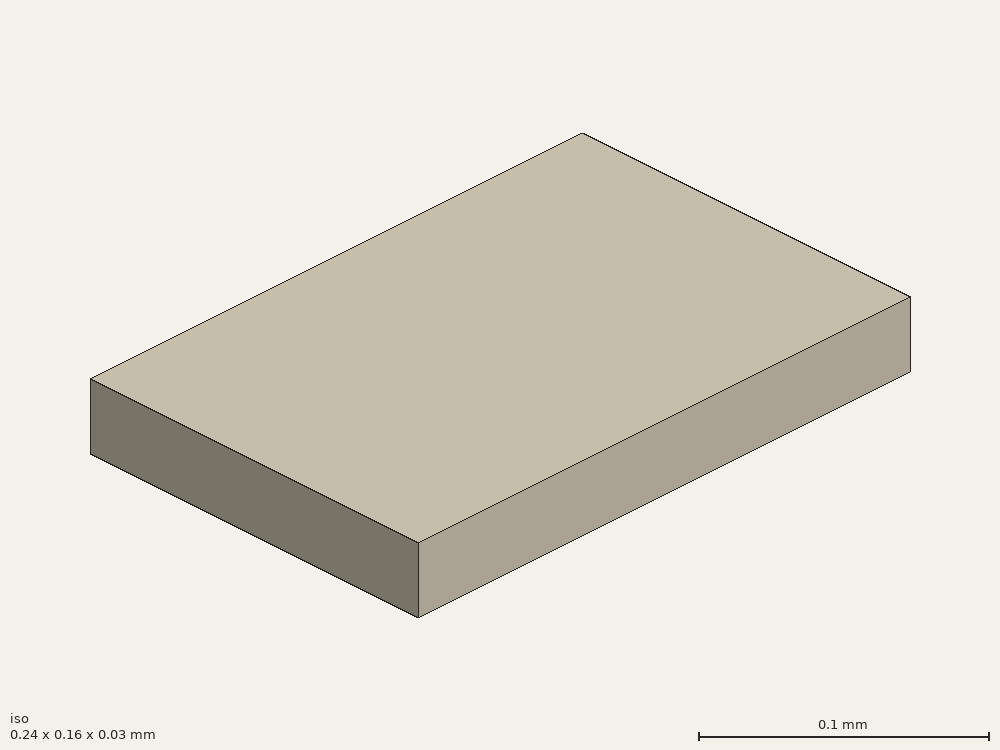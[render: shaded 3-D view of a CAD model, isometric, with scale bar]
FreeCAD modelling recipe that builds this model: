
FCSTD DOCUMENT  (FreeCAD 0.15R4671 (Git))
Label: quadrangle3
License: All rights reserved
LicenseURL: http://en.wikipedia.org/wiki/All_rights_reserved
objects: Sketcher::SketchObject×1, PartDesign::Pad×1
note: 3 computed .brp shape members not serialized (recipe doc carries the construction recipe); baked Part::Feature solids carry a one-line shape summary decoded from their .brp

FEATURE [Sketcher::SketchObject] Sketch
  sketch-geometry (4):
    g0: LineSegment StartX=0.12 StartY=0.08 StartZ=0 EndX=-0.12 EndY=0.08 EndZ=0
    g1: LineSegment StartX=-0.12 StartY=0.08 StartZ=0 EndX=-0.12 EndY=-0.08 EndZ=0
    g2: LineSegment StartX=-0.12 StartY=-0.08 StartZ=0 EndX=0.12 EndY=-0.08 EndZ=0
    g3: LineSegment StartX=0.12 StartY=-0.08 StartZ=0 EndX=0.12 EndY=0.08 EndZ=0
  constraints (13):
    c: Coincident(g0,g1)
    c: Coincident(g1,g2)
    c: Coincident(g2,g3)
    c: Coincident(g3,g0)
    c: Horizontal(g0)
    c: Horizontal(g2)
    c: Vertical(g1)
    c: Vertical(g3)
    c: Symmetric(g0,g2,g-1)
    c: Equal(g0,g2)
    c: Equal(g3,g1)
    c: DistanceY(g0,g1) = -0.16
    c: DistanceX(g0,g0) = 0.24
FEATURE [PartDesign::Pad] Pad
  Length = 0.03
  Length2 = 100
  Midplane = true
  Sketch = -> Sketch
  Type = 0
